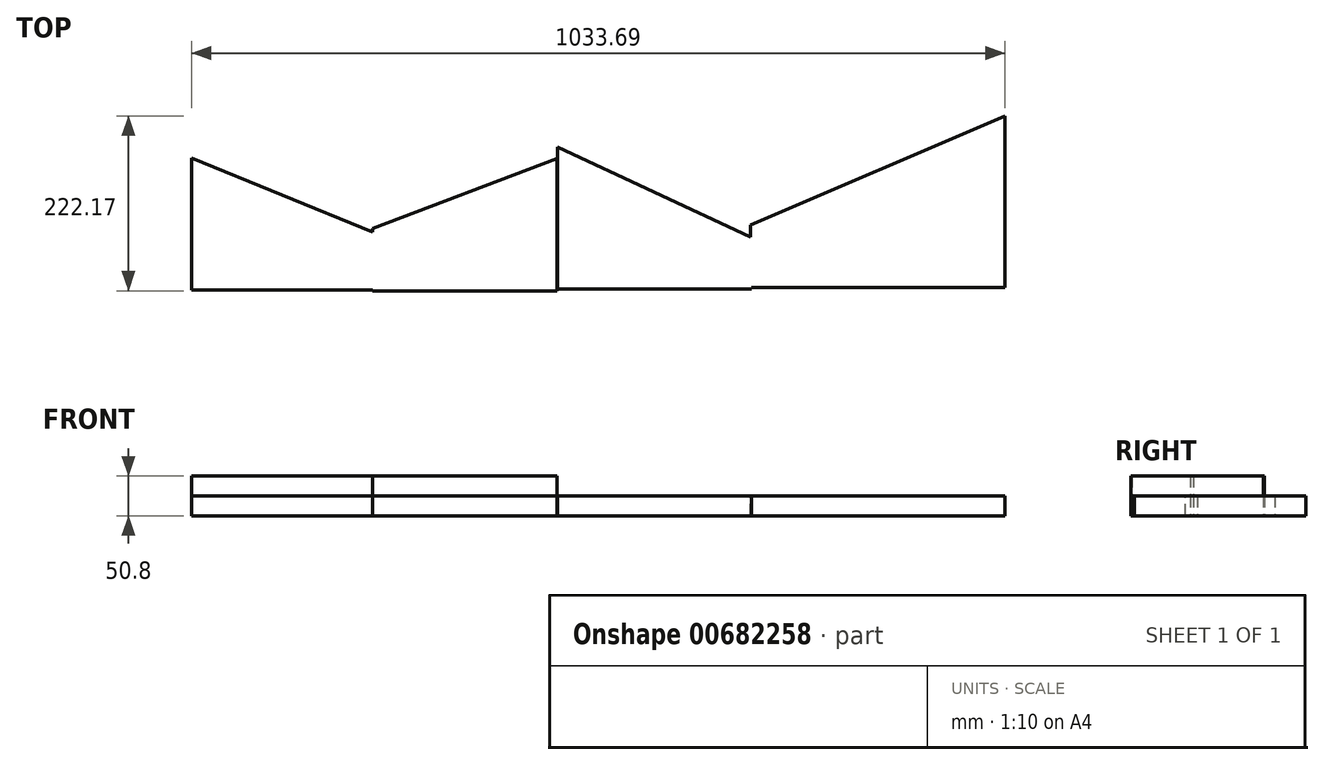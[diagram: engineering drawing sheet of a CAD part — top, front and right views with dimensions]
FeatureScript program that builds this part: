
annotation { "Feature Type Name" : "Feature", "Feature Type Description" : "" }
export const myFeature = defineFeature(function(context is Context, id is Id, definition is map)
    precondition{}
    {
        {
            var Q0;
            Q0=qCreatedBy(makeId("Top.planeOp"),FACE);
            var sketch = newSketch(context, id + "F0", { "sketchPlane" : qUnion([Q0])});
            skLineSegment(sketch, "E0.top", {"start": v(-108, -117.16) * mm, "end": v(124.53, -117.16) * mm});
            skLineSegment(sketch, "E0.left", {"start": v(-108, 50.85) * mm, "end": v(-108, -117.16) * mm});
            skLineSegment(sketch, "E0.right", {"start": v(124.53, -44.25) * mm, "end": v(124.53, -117.16) * mm});
            skLineSegment(sketch, "E1", {"start": v(-108, 50.85) * mm, "end": v(124.53, -44.25) * mm});
            skSolve(sketch);
        }
        {
            var Q0;
            Q0 = qSketchRegion(id + "F0", true);
            extrude(context, id + "F1", {"entities" : qUnion([Q0]), "depth" : 25.4 * mm, "offsetDistance" : 25.4 * mm});
        }
        {
            var Q0;
            Q0=qCreatedBy(makeId("Top.planeOp"),FACE);
            var sketch = newSketch(context, id + "F2", { "sketchPlane" : qUnion([Q0])});
            skLineSegment(sketch, "E2.top", {"start": v(121.83, -118.24) * mm, "end": v(356.16, -118.24) * mm});
            skLineSegment(sketch, "E2.left", {"start": v(121.83, -39.04) * mm, "end": v(121.83, -118.24) * mm});
            skLineSegment(sketch, "E2.right", {"start": v(356.16, 50.05) * mm, "end": v(356.16, -118.24) * mm});
            skLineSegment(sketch, "E3", {"start": v(121.83, -39.04) * mm, "end": v(356.16, 50.05) * mm});
            skSolve(sketch);
        }
        {
            var Q0;
            Q0 = qSketchRegion(id + "F2", true);
            extrude(context, id + "F3", {"entities" : qUnion([Q0]), "operationType" : NewBodyOperationType.ADD, "depth" : 25.4 * mm, "offsetDistance" : 25.4 * mm});
        }
        {
            var Q0;
            Q0=qCreatedBy(makeId("Top.planeOp"),FACE);
            var sketch = newSketch(context, id + "F4", { "sketchPlane" : qUnion([Q0])});
            skLineSegment(sketch, "E4.bottom", {"start": v(357.02, -115.58) * mm, "end": v(603.48, -115.58) * mm});
            skLineSegment(sketch, "E4.left", {"start": v(357.02, -115.58) * mm, "end": v(357.02, 64.6) * mm});
            skLineSegment(sketch, "E4.right", {"start": v(603.48, -115.58) * mm, "end": v(603.48, -50.17) * mm});
            skLineSegment(sketch, "E5", {"start": v(357.02, 64.6) * mm, "end": v(603.48, -50.17) * mm});
            skSolve(sketch);
        }
        {
            var Q0;
            Q0 = qSketchRegion(id + "F4", true);
            var Q1;
            Q1=makeQuery(id+"F3.boolean.opBoolean","MERGE",FACE,{"derivedFrom":[makeQuery(id+"F1.opExtrude","CAP_FACE",FACE,{"disambiguationData":[OSD([sQuery(id+"F0.wireOp",EDGE,"E0.top"),sQuery(id+"F0.wireOp",EDGE,"E0.left"),sQuery(id+"F0.wireOp",EDGE,"E0.right"),sQuery(id+"F0.wireOp",EDGE,"E1")])],"isStart":false}),makeQuery(id+"F3.opExtrude","CAP_FACE",FACE,{"disambiguationData":[OSD([sQuery(id+"F2.wireOp",EDGE,"E2.top"),sQuery(id+"F2.wireOp",EDGE,"E2.left"),sQuery(id+"F2.wireOp",EDGE,"E2.right"),sQuery(id+"F2.wireOp",EDGE,"E3")])],"isStart":false})]});
            extrude(context, id + "F5", {"entities" : qUnion([Q0, Q1]), "depth" : 25.4 * mm, "offsetDistance" : 25.4 * mm});
        }
        {
            var Q0;
            Q0=qCreatedBy(makeId("Top.planeOp"),FACE);
            var sketch = newSketch(context, id + "F6", { "sketchPlane" : qUnion([Q0])});
            skLineSegment(sketch, "E6.bottom", {"start": v(601.97, -114.2) * mm, "end": v(925.69, -114.2) * mm});
            skLineSegment(sketch, "E6.left", {"start": v(601.97, -114.2) * mm, "end": v(601.97, -34.23) * mm});
            skLineSegment(sketch, "E6.right", {"start": v(925.69, -114.2) * mm, "end": v(925.69, 103.93) * mm});
            skLineSegment(sketch, "E7", {"start": v(601.97, -34.23) * mm, "end": v(925.69, 103.93) * mm});
            skSolve(sketch);
        }
        {
            var Q0;
            Q0 = qSketchRegion(id + "F6", true);
            extrude(context, id + "F7", {"entities" : qUnion([Q0]), "operationType" : NewBodyOperationType.ADD, "depth" : 25.4 * mm, "offsetDistance" : 25.4 * mm});
        }
    });
